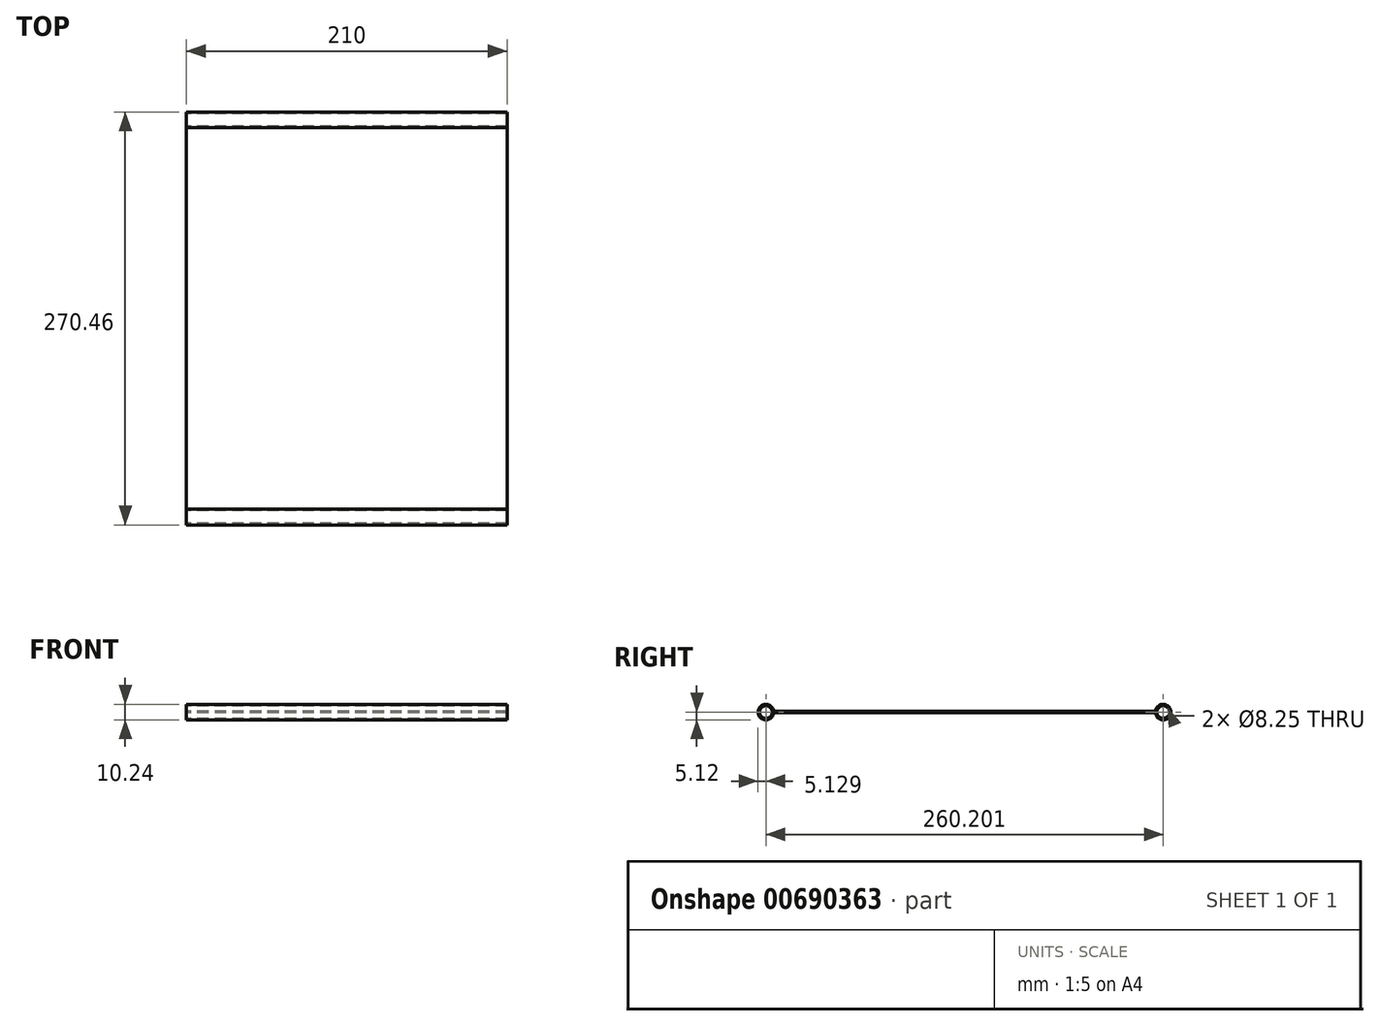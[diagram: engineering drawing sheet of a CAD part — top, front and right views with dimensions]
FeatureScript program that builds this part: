
annotation { "Feature Type Name" : "Feature", "Feature Type Description" : "" }
export const myFeature = defineFeature(function(context is Context, id is Id, definition is map)
    precondition{}
    {
        {
            var Q0;
            Q0=qCreatedBy(makeId("Top.planeOp"),FACE);
            var sketch = newSketch(context, id + "F0", { "sketchPlane" : qUnion([Q0])});
            skLineSegment(sketch, "E0.bottom", {"start": v(105, -125) * mm, "end": v(-105, -125) * mm});
            skLineSegment(sketch, "E0.top", {"start": v(105, 125) * mm, "end": v(-105, 125) * mm});
            skLineSegment(sketch, "E0.left", {"start": v(105, -125) * mm, "end": v(105, 125) * mm});
            skLineSegment(sketch, "E0.right", {"start": v(-105, -125) * mm, "end": v(-105, 125) * mm});
            skPoint(sketch, "E0.middle", {"position": v(0, 0) * mm});
            skSolve(sketch);
        }
        {
            var Q0;
            Q0=makeQuery(id+"F0.imprint","IMPRINT",FACE,{"disambiguationData":[TD([[makeQuery(id+"F0.imprint","IMPRINT",EDGE,{"derivedFrom":sQuery(id+"F0.wireOp",EDGE,"E0.bottom")}),-1.0]])]});
            extrude(context, id + "F1", {"entities" : qUnion([Q0]), "endBound" : BoundingType.SYMMETRIC, "depth" : 1 * mm, "offsetDistance" : 25 * mm});
        }
        {
            var Q0;
            Q0=qCreatedBy(makeId("Right.planeOp"),FACE);
            var sketch = newSketch(context, id + "F2", { "sketchPlane" : qUnion([Q0])});
            skCircle(sketch, "E1", {"center": v(-130.1, 0) * mm, "radius": 4.12 * mm});
            skCircle(sketch, "E2.0", {"center": v(-130.1, 0) * mm, "radius": 5.12 * mm});
            skSolve(sketch);
        }
        {
            var Q0;
            Q0=makeQuery(id+"F2.imprint","IMPRINT",FACE,{"disambiguationData":[TD([[makeQuery(id+"F2.imprint","IMPRINT",EDGE,{"derivedFrom":sQuery(id+"F2.wireOp",EDGE,"E1")}),-1.0]])]});
            var Q1;
            Q1=makeQuery(id+"F1.opExtrude","SWEPT_FACE",FACE,{"disambiguationData":[OSD([sQuery(id+"F0.wireOp",EDGE,"E0.left")])]});
            var Q2;
            Q2=makeQuery(id+"F1.opExtrude","SWEPT_FACE",FACE,{"disambiguationData":[OSD([sQuery(id+"F0.wireOp",EDGE,"E0.right")])]});
            extrude(context, id + "F3", {"entities" : qUnion([Q0]), "operationType" : NewBodyOperationType.ADD, "endBound" : BoundingType.UP_TO_SURFACE, "depth" : 25 * mm, "endBoundEntityFace" : qUnion([Q1]), "offsetDistance" : 25 * mm, "hasSecondDirection" : true, "secondDirectionBound" : SecondDirectionBoundingType.UP_TO_SURFACE, "secondDirectionOppositeDirection" : true, "secondDirectionDepth" : 25 * mm, "secondDirectionBoundEntityFace" : qUnion([Q2])});
        }
        {
            var Q0;
            Q0=makeQuery(id+"F1.opExtrude","SWEPT_BODY",BODY,{"disambiguationData":[OSD([sQuery(id+"F0.wireOp",EDGE,"E0.bottom"),sQuery(id+"F0.wireOp",EDGE,"E0.top"),sQuery(id+"F0.wireOp",EDGE,"E0.left"),sQuery(id+"F0.wireOp",EDGE,"E0.right")])]});
            var Q1;
            Q1=qCreatedBy(makeId("Front.planeOp"),FACE);
            mirror(context, id + "F4", {"operationType" : NewBodyOperationType.ADD, "entities" : qUnion([Q0]), "mirrorPlane" : qUnion([Q1])});
        }
    });
